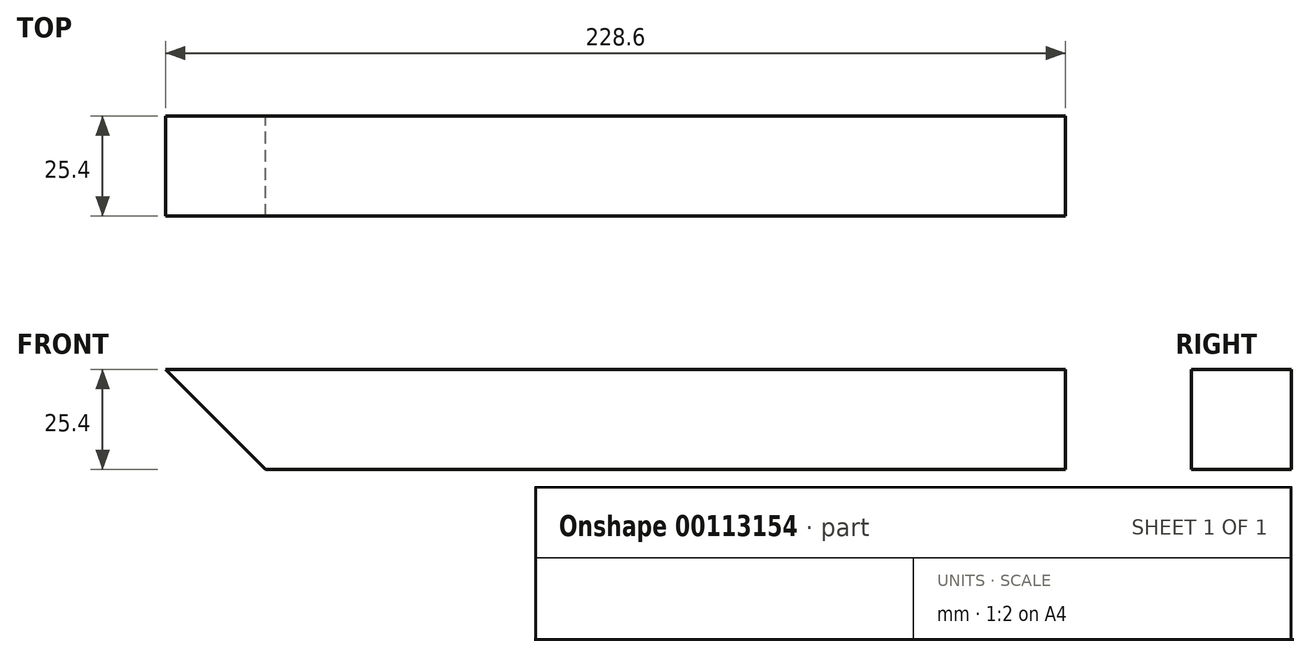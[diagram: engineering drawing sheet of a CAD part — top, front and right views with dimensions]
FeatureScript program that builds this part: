
annotation { "Feature Type Name" : "Feature", "Feature Type Description" : "" }
export const myFeature = defineFeature(function(context is Context, id is Id, definition is map)
    precondition{}
    {
        {
            var Q0;
            Q0=qCreatedBy(makeId("Front.planeOp"),FACE);
            var sketch = newSketch(context, id + "F0", { "sketchPlane" : qUnion([Q0])});
            skLineSegment(sketch, "E0.bottom", {"start": v(-179.43, 36.77) * mm, "end": v(36.47, 36.77) * mm});
            skLineSegment(sketch, "E0.top", {"start": v(-179.43, 11.37) * mm, "end": v(36.47, 11.37) * mm});
            skLineSegment(sketch, "E0.left", {"start": v(-179.43, 36.77) * mm, "end": v(-179.43, 11.37) * mm});
            skLineSegment(sketch, "E0.right", {"start": v(36.47, 36.77) * mm, "end": v(36.47, 11.37) * mm});
            skSolve(sketch);
        }
        {
            var Q0;
            Q0=makeQuery(id+"F0.imprint","IMPRINT",FACE,{"disambiguationData":[TD([[makeQuery(id+"F0.imprint","IMPRINT",EDGE,{"derivedFrom":sQuery(id+"F0.wireOp",EDGE,"E0.bottom")}),-1.0]])]});
            extrude(context, id + "F1", {"entities" : qUnion([Q0]), "oppositeDirection" : true, "depth" : 25.4 * mm});
        }
        {
            var Q0;
            Q0=makeQuery(id+"F1.opExtrude","SWEPT_FACE",FACE,{"disambiguationData":[OSD([sQuery(id+"F0.wireOp",EDGE,"E0.right")])]});
            extrude(context, id + "F2", {"entities" : qUnion([Q0]), "operationType" : NewBodyOperationType.ADD, "depth" : 12.7 * mm});
        }
        {
            var Q0;
            Q0=makeQuery(id+"F1.opExtrude","SWEPT_EDGE",EDGE,{"disambiguationData":[OSD([sQuery(id+"F0.wireOp",EDGE,"E0.top"),sQuery(id+"F0.wireOp",EDGE,"E0.left")])]});
            chamfer(context, id + "F3", {"entities" : qUnion([Q0]), "chamferType" : ChamferType.OFFSET_ANGLE, "width" : 25.4 * mm, "oppositeDirection" : false, "angle" : 45 * degree, "tangentPropagation" : true});
        }
    });
